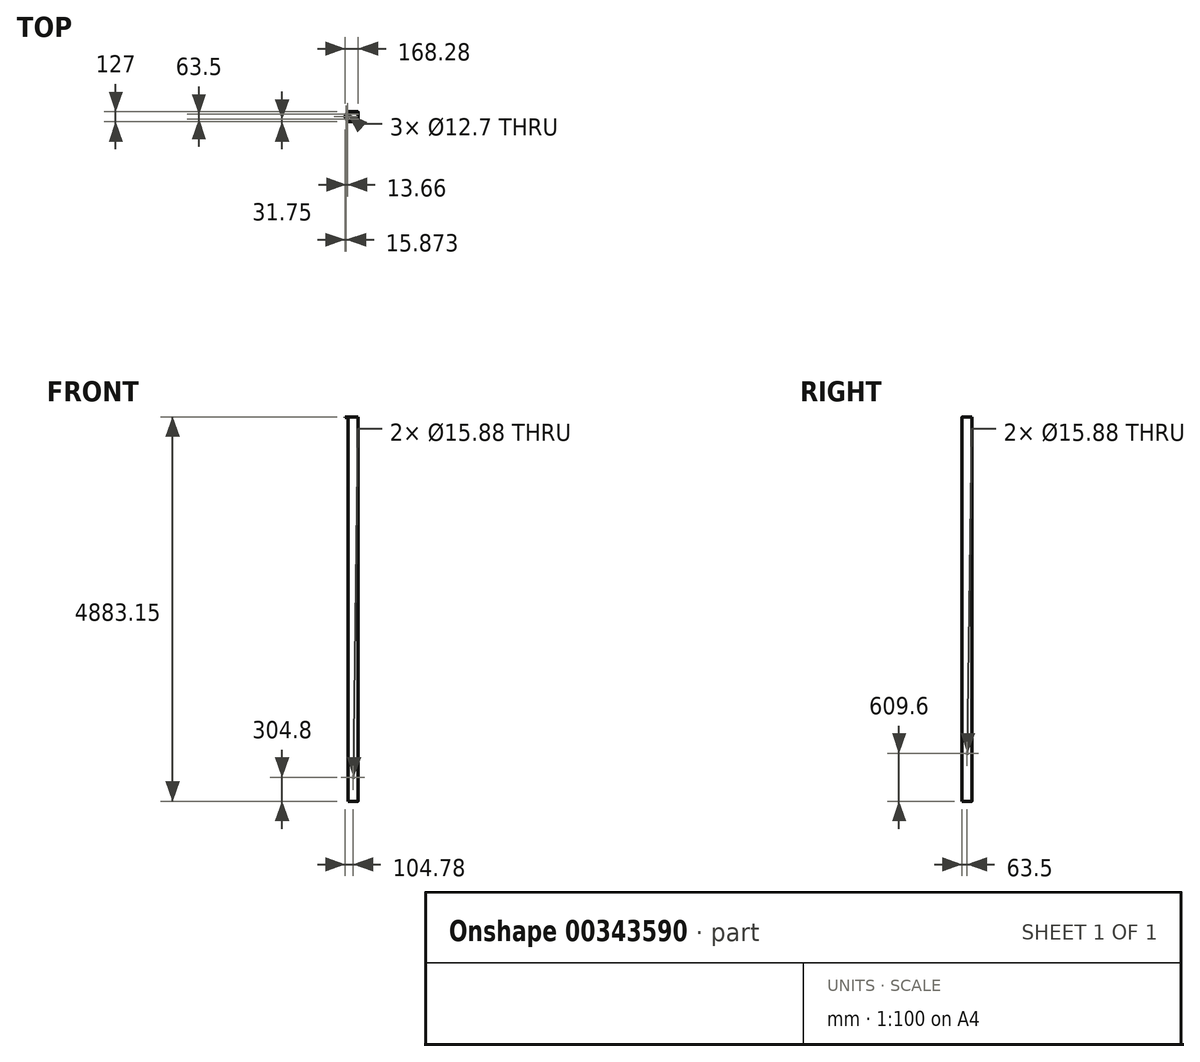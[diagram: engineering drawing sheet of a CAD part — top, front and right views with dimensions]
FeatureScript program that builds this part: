
annotation { "Feature Type Name" : "Feature", "Feature Type Description" : "" }
export const myFeature = defineFeature(function(context is Context, id is Id, definition is map)
    precondition{}
    {
        {
            var Q0;
            Q0=qCreatedBy(makeId("Top.planeOp"),FACE);
            var sketch = newSketch(context, id + "F0", { "sketchPlane" : qUnion([Q0])});
            skLineSegment(sketch, "E0.bottom", {"start": v(0, 0) * mm, "end": v(-127, 0) * mm});
            skLineSegment(sketch, "E0.top", {"start": v(0, -127) * mm, "end": v(-127, -127) * mm});
            skLineSegment(sketch, "E0.left", {"start": v(0, 0) * mm, "end": v(0, -127) * mm});
            skLineSegment(sketch, "E0.right", {"start": v(-127, 0) * mm, "end": v(-127, -127) * mm});
            skLineSegment(sketch, "E1", {"start": v(-127, -127) * mm, "end": v(0, 0) * mm, "construction": true});
            skLineSegment(sketch, "E2", {"start": v(0, -127) * mm, "end": v(-127, 0) * mm, "construction": true});
            skLineSegment(sketch, "E3.bottom", {"start": v(-120.65, -120.65) * mm, "end": v(-6.35, -120.65) * mm});
            skLineSegment(sketch, "E3.top", {"start": v(-120.65, -6.35) * mm, "end": v(-6.35, -6.35) * mm});
            skLineSegment(sketch, "E3.left", {"start": v(-120.65, -120.65) * mm, "end": v(-120.65, -6.35) * mm});
            skLineSegment(sketch, "E3.right", {"start": v(-6.35, -120.65) * mm, "end": v(-6.35, -6.35) * mm});
            skPoint(sketch, "E3.middle", {"position": v(-63.5, -63.5) * mm});
            skSolve(sketch);
        }
        {
            var Q0;
            Q0=makeQuery(id+"F0.imprint","IMPRINT",FACE,{"disambiguationData":[TD([[makeQuery(id+"F0.imprint","IMPRINT",EDGE,{"derivedFrom":sQuery(id+"F0.wireOp",EDGE,"E0.bottom")}),1.0]])]});
            extrude(context, id + "F1", {"entities" : qUnion([Q0]), "depth" : 4876.8 * mm});
        }
        {
            var Q0;
            Q0=makeQuery(id+"F1.opExtrude","SWEPT_EDGE",EDGE,{"disambiguationData":[OSD([sQuery(id+"F0.wireOp",EDGE,"E0.bottom"),sQuery(id+"F0.wireOp",EDGE,"E0.right")])]});
            var Q1;
            Q1=makeQuery(id+"F1.opExtrude","SWEPT_EDGE",EDGE,{"disambiguationData":[OSD([sQuery(id+"F0.wireOp",EDGE,"E3.top"),sQuery(id+"F0.wireOp",EDGE,"E3.right")])]});
            var Q2;
            Q2=makeQuery(id+"F1.opExtrude","SWEPT_EDGE",EDGE,{"disambiguationData":[OSD([sQuery(id+"F0.wireOp",EDGE,"E0.top"),sQuery(id+"F0.wireOp",EDGE,"E0.left")])]});
            var Q3;
            Q3=makeQuery(id+"F1.opExtrude","SWEPT_EDGE",EDGE,{"disambiguationData":[OSD([sQuery(id+"F0.wireOp",EDGE,"E0.top"),sQuery(id+"F0.wireOp",EDGE,"E0.right")])]});
            var Q4;
            Q4=makeQuery(id+"F1.opExtrude","SWEPT_EDGE",EDGE,{"disambiguationData":[OSD([sQuery(id+"F0.wireOp",EDGE,"E3.top"),sQuery(id+"F0.wireOp",EDGE,"E3.left")])]});
            var Q5;
            Q5=makeQuery(id+"F1.opExtrude","SWEPT_EDGE",EDGE,{"disambiguationData":[OSD([sQuery(id+"F0.wireOp",EDGE,"E3.bottom"),sQuery(id+"F0.wireOp",EDGE,"E3.left")])]});
            var Q6;
            Q6=makeQuery(id+"F1.opExtrude","SWEPT_EDGE",EDGE,{"disambiguationData":[OSD([sQuery(id+"F0.wireOp",EDGE,"E0.bottom"),sQuery(id+"F0.wireOp",EDGE,"E0.left")])]});
            var Q7;
            Q7=makeQuery(id+"F1.opExtrude","SWEPT_EDGE",EDGE,{"disambiguationData":[OSD([sQuery(id+"F0.wireOp",EDGE,"E3.bottom"),sQuery(id+"F0.wireOp",EDGE,"E3.right")])]});
            fillet(context, id + "F2", {"entities" : qUnion([Q0, Q1, Q2, Q3, Q4, Q5, Q6, Q7]), "radius" : 5.08 * mm, "tangentPropagation" : true, "allowEdgeOverflow" : false});
        }
        {
            var Q0;
            Q0=makeQuery(id+"F1.opExtrude","SWEPT_FACE",FACE,{"disambiguationData":[OSD([sQuery(id+"F0.wireOp",EDGE,"E0.bottom")])]});
            var sketch = newSketch(context, id + "F3", { "sketchPlane" : qUnion([Q0])});
            skLineSegment(sketch, "E4", {"start": v(63.5, 0) * mm, "end": v(63.5, 4876.8) * mm});
            skLineSegment(sketch, "E5", {"start": v(63.5, 0) * mm, "end": v(63.5, 304.8) * mm, "construction": true});
            skCircle(sketch, "E6", {"center": v(63.5, 304.8) * mm, "radius": 7.94 * mm});
            skSolve(sketch);
        }
        {
            var Q0;
            Q0 = qSketchRegion(id + "F3", true);
            extrude(context, id + "F4", {"entities" : qUnion([Q0]), "operationType" : NewBodyOperationType.REMOVE, "oppositeDirection" : true, "depth" : 127 * mm});
        }
        {
            var Q0;
            Q0=makeQuery(id+"F1.opExtrude","SWEPT_FACE",FACE,{"disambiguationData":[OSD([sQuery(id+"F0.wireOp",EDGE,"E0.right")])]});
            var sketch = newSketch(context, id + "F5", { "sketchPlane" : qUnion([Q0])});
            skLineSegment(sketch, "E7", {"start": v(63.5, 0) * mm, "end": v(63.5, 609.6) * mm, "construction": true});
            skCircle(sketch, "E8", {"center": v(63.5, 609.6) * mm, "radius": 7.94 * mm});
            skSolve(sketch);
        }
        {
            var Q0;
            Q0 = qSketchRegion(id + "F5", true);
            extrude(context, id + "F6", {"entities" : qUnion([Q0]), "operationType" : NewBodyOperationType.REMOVE, "oppositeDirection" : true, "depth" : 127 * mm});
        }
        {
            var Q0;
            Q0=makeQuery(id+"F1.opExtrude","CAP_FACE",FACE,{"disambiguationData":[OSD([sQuery(id+"F0.wireOp",EDGE,"E0.bottom"),sQuery(id+"F0.wireOp",EDGE,"E0.top"),sQuery(id+"F0.wireOp",EDGE,"E0.left"),sQuery(id+"F0.wireOp",EDGE,"E0.right"),sQuery(id+"F0.wireOp",EDGE,"E3.bottom"),sQuery(id+"F0.wireOp",EDGE,"E3.top"),sQuery(id+"F0.wireOp",EDGE,"E3.left"),sQuery(id+"F0.wireOp",EDGE,"E3.right")])],"isStart":false});
            var sketch = newSketch(context, id + "F7", { "sketchPlane" : qUnion([Q0])});
            skLineSegment(sketch, "E9.bottom", {"start": v(0, -127) * mm, "end": v(-121.92, -127) * mm});
            skLineSegment(sketch, "E9.top", {"start": v(0, 0) * mm, "end": v(-121.92, 0) * mm});
            skLineSegment(sketch, "E9.left", {"start": v(0, -127) * mm, "end": v(0, 0) * mm});
            skLineSegment(sketch, "E10", {"start": v(-168.28, -63.5) * mm, "end": v(-156.69, -95.25) * mm, "construction": true});
            skLineSegment(sketch, "E11", {"start": v(-168.28, -63.5) * mm, "end": v(-156.69, -31.75) * mm, "construction": true});
            skLineSegment(sketch, "E12", {"start": v(-121.92, -127) * mm, "end": v(-156.69, -95.25) * mm});
            skLineSegment(sketch, "E13", {"start": v(-156.69, -95.25) * mm, "end": v(-168.28, -63.5) * mm});
            skLineSegment(sketch, "E14", {"start": v(-168.28, -63.5) * mm, "end": v(-156.69, -31.75) * mm});
            skLineSegment(sketch, "E15", {"start": v(-156.69, -31.75) * mm, "end": v(-121.92, 0) * mm});
            skPoint(sketch, "E16.orphan", {"position": v(-145.1, 0) * mm});
            skPoint(sketch, "E17.orphan", {"position": v(-145.1, -127) * mm});
            skPoint(sketch, "E18.orphan", {"position": v(-168.28, 0) * mm});
            skPoint(sketch, "E19.trimOffspring.end.orphan", {"position": v(-168.28, -127) * mm});
            skSolve(sketch);
        }
        {
            var Q0;
            {var subQ8=sQuery(id+"F7.wireOp",EDGE,"E13");Q0=makeQuery(id+"F7.imprint","IMPRINT",FACE,{"disambiguationData":[TD([[makeQuery(id+"F7.imprint","IMPRINT",EDGE,{"derivedFrom":subQ8}),-1.0]])]});}
            var Q1;
            {var subQ4=sQuery(id+"F0.wireOp",EDGE,"E0.right");var subQ21=makeQuery(id+"F1.opExtrude","CAP_EDGE",EDGE,{"disambiguationData":[OSD([subQ4])],"isStart":false});Q1=makeQuery(id+"F7.imprint","IMPRINT",FACE,{"disambiguationData":[TD([[makeQuery(id+"F7.imprint","IMPRINT",EDGE,{"derivedFrom":subQ21}),1.0]])]});}
            var Q2;
            {var subQ3=sQuery(id+"F0.wireOp",EDGE,"E3.bottom");Q2=makeQuery(id+"F7.imprint","IMPRINT",FACE,{"disambiguationData":[TD([[makeQuery(id+"F7.imprint","IMPRINT",EDGE,{"derivedFrom":makeQuery(id+"F1.opExtrude","CAP_EDGE",EDGE,{"disambiguationData":[OSD([subQ3])],"isStart":false})}),1.0]])]});}
            extrude(context, id + "F8", {"entities" : qUnion([Q0, Q1, Q2]), "operationType" : NewBodyOperationType.ADD, "depth" : 6.35 * mm});
        }
        {
            var Q0;
            Q0=makeQuery(id+"F8.opExtrude","CAP_FACE",FACE,{"disambiguationData":[OSD([sQuery(id+"F0.wireOp",EDGE,"E0.bottom"),sQuery(id+"F0.wireOp",EDGE,"E0.top"),sQuery(id+"F0.wireOp",EDGE,"E0.left"),sQuery(id+"F0.wireOp",EDGE,"E0.right"),sQuery(id+"F0.wireOp",EDGE,"E3.bottom"),sQuery(id+"F0.wireOp",EDGE,"E3.top"),sQuery(id+"F0.wireOp",EDGE,"E3.left"),sQuery(id+"F0.wireOp",EDGE,"E3.right"),sQuery(id+"F7.wireOp",EDGE,"E9.bottom"),sQuery(id+"F7.wireOp",EDGE,"E9.top"),sQuery(id+"F7.wireOp",EDGE,"E9.left"),sQuery(id+"F7.wireOp",EDGE,"E12"),sQuery(id+"F7.wireOp",EDGE,"E13"),sQuery(id+"F7.wireOp",EDGE,"E14"),sQuery(id+"F7.wireOp",EDGE,"E15")])],"isStart":false});
            var sketch = newSketch(context, id + "F9", { "sketchPlane" : qUnion([Q0])});
            skCircle(sketch, "E20", {"center": v(-152.4, -63.5) * mm, "radius": 6.35 * mm});
            skLineSegment(sketch, "E21", {"start": v(-138.75, -31.75) * mm, "end": v(-138.75, -27.53) * mm, "construction": true});
            skCircle(sketch, "E22", {"center": v(-138.75, -31.75) * mm, "radius": 6.35 * mm});
            skCircle(sketch, "E23", {"center": v(-138.75, -95.25) * mm, "radius": 6.35 * mm});
            skSolve(sketch);
        }
        {
            var Q0;
            Q0=makeQuery(id+"F9.imprint","IMPRINT",FACE,{"disambiguationData":[TD([[makeQuery(id+"F9.imprint","IMPRINT",EDGE,{"derivedFrom":sQuery(id+"F9.wireOp",EDGE,"E22")}),1.0]])]});
            var Q1;
            Q1=makeQuery(id+"F9.imprint","IMPRINT",FACE,{"disambiguationData":[TD([[makeQuery(id+"F9.imprint","IMPRINT",EDGE,{"derivedFrom":sQuery(id+"F9.wireOp",EDGE,"E20")}),1.0]])]});
            var Q2;
            Q2=makeQuery(id+"F9.imprint","IMPRINT",FACE,{"disambiguationData":[TD([[makeQuery(id+"F9.imprint","IMPRINT",EDGE,{"derivedFrom":sQuery(id+"F9.wireOp",EDGE,"E23")}),1.0]])]});
            extrude(context, id + "F10", {"entities" : qUnion([Q0, Q1, Q2]), "operationType" : NewBodyOperationType.REMOVE, "oppositeDirection" : true, "depth" : 6.35 * mm});
        }
    });
